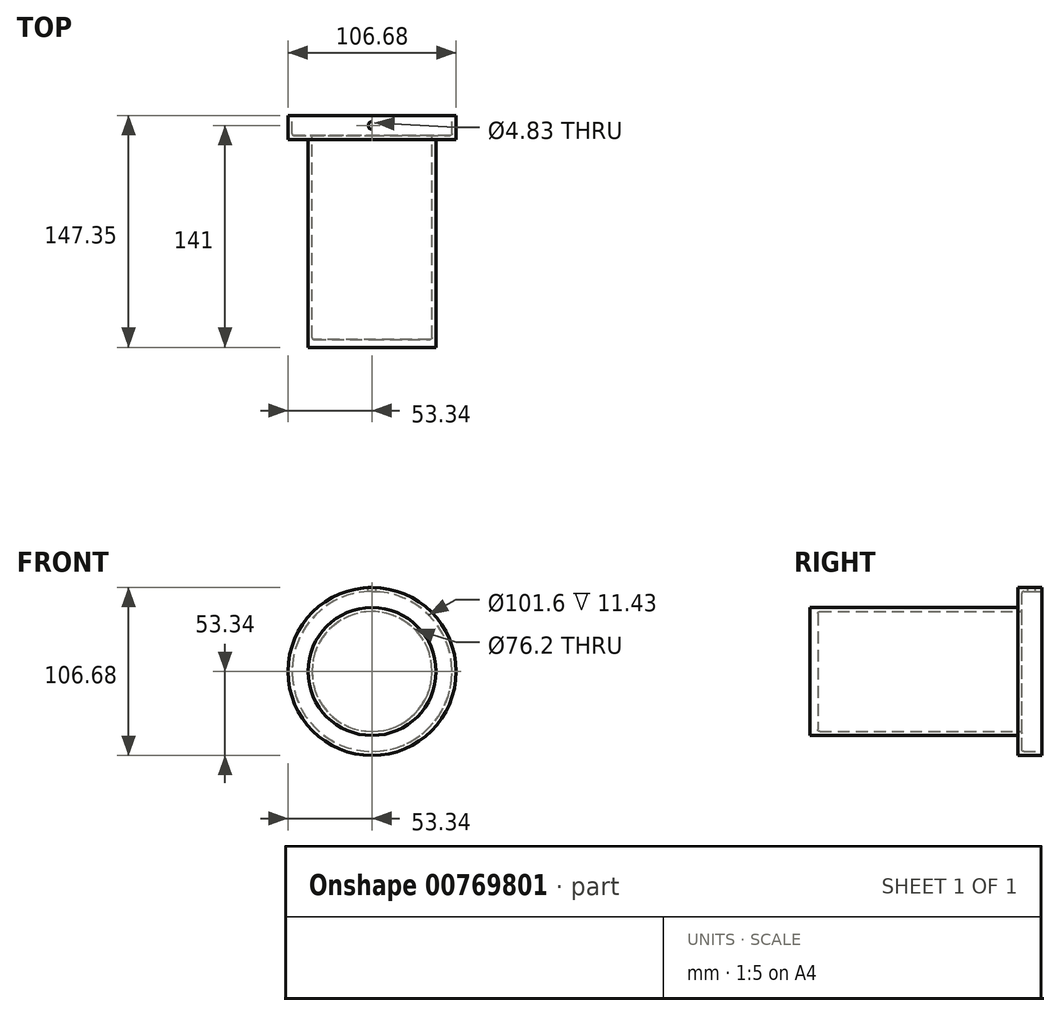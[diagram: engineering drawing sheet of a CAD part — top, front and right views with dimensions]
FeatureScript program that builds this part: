
annotation { "Feature Type Name" : "Feature", "Feature Type Description" : "" }
export const myFeature = defineFeature(function(context is Context, id is Id, definition is map)
    precondition{}
    {
        {
            var Q0;
            Q0=qCreatedBy(makeId("Right.planeOp"),FACE);
            var sketch = newSketch(context, id + "F0", { "sketchPlane" : qUnion([Q0])});
            skLineSegment(sketch, "E0", {"start": v(6.35, 50.8) * mm, "end": v(-6.35, 50.8) * mm});
            skLineSegment(sketch, "E1", {"start": v(-6.35, 50.8) * mm, "end": v(-6.35, 38.1) * mm});
            skLineSegment(sketch, "E2", {"start": v(-6.35, 38.1) * mm, "end": v(-135.92, 38.1) * mm});
            skLineSegment(sketch, "E3.0", {"start": v(-8.89, 40.64) * mm, "end": v(-135.92, 40.64) * mm});
            skLineSegment(sketch, "E3.1", {"start": v(-8.9, 53.34) * mm, "end": v(-8.89, 40.64) * mm});
            skLineSegment(sketch, "E3.2", {"start": v(6.35, 53.34) * mm, "end": v(-8.9, 53.34) * mm});
            skLineSegment(sketch, "E4", {"start": v(6.35, 53.34) * mm, "end": v(6.35, 50.8) * mm});
            skLineSegment(sketch, "E5", {"start": v(0, 0) * mm, "end": v(-119.95, 0) * mm, "construction": true});
            skLineSegment(sketch, "E6", {"start": v(-135.92, 40.64) * mm, "end": v(-141, 40.64) * mm});
            skLineSegment(sketch, "E7", {"start": v(-141, 40.64) * mm, "end": v(-141, 0) * mm});
            skLineSegment(sketch, "E8", {"start": v(-141, 0) * mm, "end": v(-135.92, 0) * mm});
            skLineSegment(sketch, "E9", {"start": v(-135.92, 0) * mm, "end": v(-135.92, 38.1) * mm});
            skLineSegment(sketch, "E10", {"start": v(-135.92, 38.1) * mm, "end": v(-135.92, 38.1) * mm});
            skSolve(sketch);
        }
        {
            var Q0;
            Q0 = qSketchRegion(id + "F0", true);
            var Q1;
            Q1=sQuery(id+"F0.wireOp",EDGE,"E5");
            revolve(context, id + "F1", {"surfaceOperationType" : NewSurfaceOperationType.NEW, "entities" : qUnion([Q0]), "axis" : qUnion([Q1]), "revolveType" : RevolveType.FULL});
        }
        {
            var Q0;
            Q0=makeQuery(id+"F1.opRevolve","SWEPT_EDGE",EDGE,{"disambiguationData":[OSD([sQuery(id+"F0.wireOp",EDGE,"E1"),sQuery(id+"F0.wireOp",EDGE,"E2")])]});
            var Q1;
            Q1=makeQuery(id+"F1.opRevolve","SWEPT_EDGE",EDGE,{"disambiguationData":[OSD([sQuery(id+"F0.wireOp",EDGE,"E0"),sQuery(id+"F0.wireOp",EDGE,"E1")])]});
            var Q2;
            Q2=makeQuery(id+"F1.opRevolve","SWEPT_EDGE",EDGE,{"disambiguationData":[OSD([sQuery(id+"F0.wireOp",EDGE,"E3.0"),sQuery(id+"F0.wireOp",EDGE,"E3.1")])]});
            var Q3;
            Q3=makeQuery(id+"F1.opRevolve","SWEPT_EDGE",EDGE,{"disambiguationData":[OSD([sQuery(id+"F0.wireOp",EDGE,"E9"),sQuery(id+"F0.wireOp",EDGE,"E10")])]});
            fillet(context, id + "F2", {"entities" : qUnion([Q0, Q1, Q2, Q3]), "radius" : 1.27 * mm, "tangentPropagation" : true, "allowEdgeOverflow" : false});
        }
        {
            var Q0;
            Q0=qCreatedBy(makeId("Top.planeOp"),FACE);
            cPlane(context, id + "F3", {"entities" : qUnion([Q0]), "cplaneType" : CPlaneType.OFFSET, "offset" : 53.34 * mm, "width" : 152.4 * mm, "height" : 152.4 * mm});
        }
        {
            var Q0;
            Q0=qCreatedBy(id+"F3.planeOp",FACE);
            var sketch = newSketch(context, id + "F4", { "sketchPlane" : qUnion([Q0])});
            skPoint(sketch, "E11", {"position": v(0, 0) * mm});
            skSolve(sketch);
        }
        {
            var Q0;
            Q0=sQuery(id+"F4.wireOp",VERTEX,"E11");
            var Q1;
            Q1=makeQuery(id+"F1.opRevolve","SWEPT_BODY",BODY,{"disambiguationData":[OSD([sQuery(id+"F0.wireOp",EDGE,"E0"),sQuery(id+"F0.wireOp",EDGE,"E1"),sQuery(id+"F0.wireOp",EDGE,"E2"),sQuery(id+"F0.wireOp",EDGE,"E3.0"),sQuery(id+"F0.wireOp",EDGE,"E3.1"),sQuery(id+"F0.wireOp",EDGE,"E3.2"),sQuery(id+"F0.wireOp",EDGE,"E4"),sQuery(id+"F0.wireOp",EDGE,"E6"),sQuery(id+"F0.wireOp",EDGE,"E7"),sQuery(id+"F0.wireOp",EDGE,"E8"),sQuery(id+"F0.wireOp",EDGE,"E9")])]});
            hole(context, id + "F5", {"style" : HoleStyle.SIMPLE, "endStyle" : HoleEndStyle.BLIND, "holeDiameter" : 4.83 * mm, "majorDiameter" : 6.35 * mm, "holeDepth" : 7.62 * mm, "isTappedThrough" : true, "tappedDepth" : 12.7 * mm, "tapClearance" : 3, "locations" : qUnion([Q0]), "scope" : qUnion([Q1])});
        }
    });
